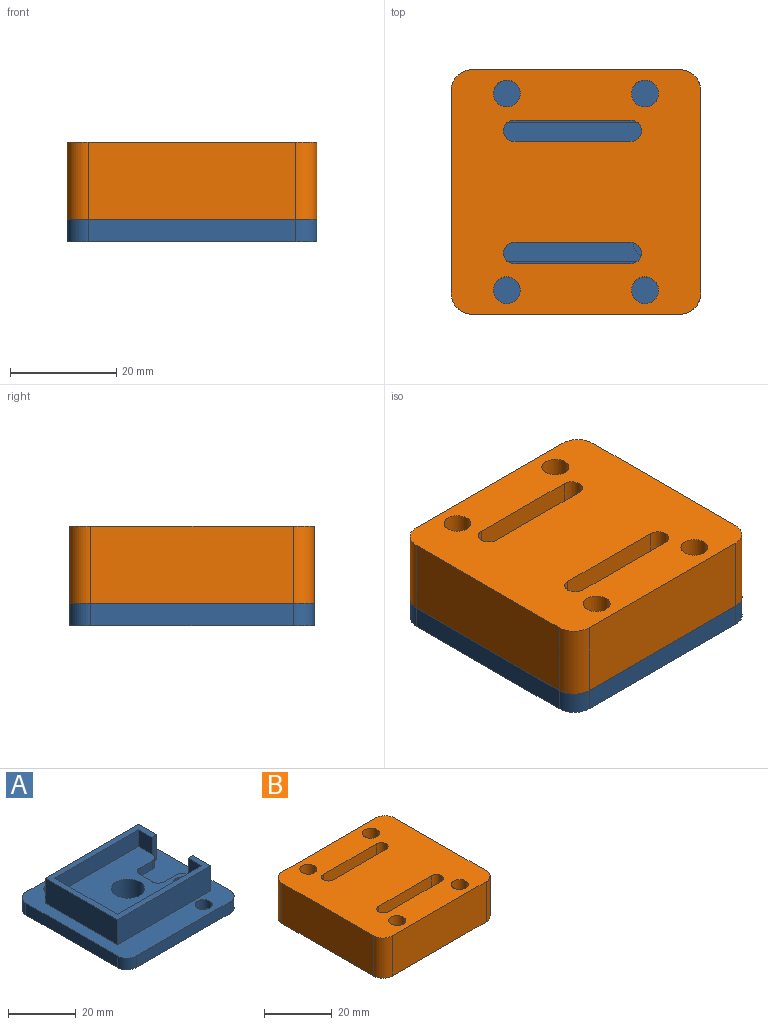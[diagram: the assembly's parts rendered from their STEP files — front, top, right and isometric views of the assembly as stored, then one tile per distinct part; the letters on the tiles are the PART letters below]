
ASSEMBLY  parts=2 mates=1
PART A: 38 faces, bbox 47x46x13.2 mm
  f0: plane 5x3mm, normal (0,-1,0), area 15mm2, adj f1,f6,f7,f21
  f1: cylinder r=2.5mm len=3mm, axis (0,0,-1), area 11.8mm2, adj f0,f7,f15,f21
  f2: cylinder r=2.5mm len=3mm, axis (0,0,-1), area 11.8mm2, adj f3,f7,f14,f21
  f3: plane 5x3mm, normal (0,1,0), area 15mm2, adj f2,f4,f7,f21
  f4: cylinder r=2.5mm len=3mm, axis (0,0,-1), area 11.8mm2, adj f3,f5,f7,f21
  f5: plane 5x3mm, normal (1,0,0), area 15mm2, adj f4,f6,f7,f21
  f6: cylinder r=2.5mm len=3mm, axis (0,0,-1), area 11.8mm2, adj f0,f5,f7,f21
  f7: plane 35x26mm, normal (0,0,1), area 706.3mm2, adj f0,f1,f2,f3,f4,f5,f6,f8
  f8: plane 35x6mm, normal (0,-1,0), area 210mm2, adj f7,f9,f11,f20
  f9: plane 26x6mm, normal (1,0,0), area 156mm2, adj f7,f8,f10,f20
  f10: plane 35x6mm, normal (0,1,0), area 210mm2, adj f7,f9,f12,f20
  f11: plane 6x5.5mm, normal (-1,0,0), area 33mm2, adj f7,f8,f15,f20
  f12: plane 6x5.5mm, normal (-1,0,0), area 33mm2, adj f7,f10,f14,f20
  f13: plane 9x7.5mm, normal (1,0,0), area 67.5mm2, adj f14,f19,f20,f21
  f14: plane 9x2mm, normal (0,1,0), area 18mm2, adj f2,f12,f13,f20,f21
  f15: plane 9x2mm, normal (0,-1,0), area 18mm2, adj f1,f11,f16,f20,f21
  f16: plane 9x7.5mm, normal (1,0,0), area 67.5mm2, adj f15,f17,f20,f21
  f17: plane 39x9mm, normal (0,1,0), area 351mm2, adj f16,f18,f20,f21
  f18: plane 30x9mm, normal (-1,0,0), area 270mm2, adj f17,f19,f20,f21
  f19: plane 39x9mm, normal (0,-1,0), area 351mm2, adj f13,f18,f20,f21
  f20: plane 39x30mm, normal (0,0,1), area 230mm2, adj f8,f9,f10,f11,f12,f13,f14,f15
  f21: plane 47x46mm, normal (0,0,1), area 1068.2mm2, adj f0,f1,f2,f3,f4,f5,f6,f13
  f22: plane 39x4.2mm, normal (0,1,0), area 163.8mm2, adj f21,f23,f31,f35
  f23: cylinder r=4mm len=4.2mm, axis (0,0,1), area 26.4mm2, adj f21,f22,f24,f35
  f24: plane 38x4.2mm, normal (-1,0,0), area 159.6mm2, adj f21,f23,f25,f35
  f25: cylinder r=4mm len=4.2mm, axis (0,0,1), area 26.4mm2, adj f21,f24,f26,f35
  f26: plane 39x4.2mm, normal (0,-1,0), area 163.8mm2, adj f21,f25,f27,f35
  f27: cylinder r=4mm len=4.2mm, axis (0,0,1), area 26.4mm2, adj f21,f26,f28,f35
  f28: plane 38x4.2mm, normal (1,0,0), area 159.6mm2, adj f21,f27,f31,f35
  f29: cylinder r=2.52mm len=5.05mm, axis (0,0,1), area 50.8mm2, adj f21,f33
  f30: cylinder r=2.52mm len=5.05mm, axis (0,0,1), area 50.8mm2, adj f21,f34
  f31: cylinder r=4mm len=4.2mm, axis (0,0,1), area 26.4mm2, adj f21,f22,f28,f35
  f32: cylinder r=4.9mm len=9.8mm, axis (0,0,-1), area 221.7mm2, adj f7,f35
  f33: plane 5.05x5.05mm, normal (0,0,1), area 20mm2, adj f29
  f34: plane 5.05x5.05mm, normal (0,0,1), area 20mm2, adj f30
  f35: plane 47x46mm, normal (0,0,-1), area 2072.8mm2, adj f22,f23,f24,f25,f26,f27,f28,f31
  f36: cylinder r=3mm len=6mm, axis (0,0,1), area 56.5mm2, adj f7,f37
  f37: plane 6x6mm, normal (0,0,1), area 28.3mm2, adj f36
PART B: 32 faces, bbox 47x46x14.5 mm
  f0: plane 39.3x9.5mm, normal (0,-1,0), area 373.4mm2, adj f1,f14,f15,f16
  f1: plane 10.15x9.5mm, normal (-1,0,0), area 74mm2, adj f0,f2,f15,f16,f27
  f2: plane 7x3.85mm, normal (0,-1,0), area 27mm2, adj f1,f10,f15,f27
  f3: cylinder r=4mm len=14.5mm, axis (0,0,-1), area 91.1mm2, adj f4,f10,f15,f21
  f4: plane 39x14.5mm, normal (0,1,0), area 565.5mm2, adj f3,f5,f15,f21
  f5: cylinder r=4mm len=14.5mm, axis (0,0,-1), area 91.1mm2, adj f4,f6,f15,f21
  f6: plane 38x14.5mm, normal (-1,0,0), area 551mm2, adj f5,f7,f15,f21
  f7: cylinder r=4mm len=14.5mm, axis (0,0,-1), area 91.1mm2, adj f6,f8,f15,f21
  f8: plane 39x14.5mm, normal (0,-1,0), area 565.5mm2, adj f7,f9,f15,f21
  f9: cylinder r=4mm len=14.5mm, axis (0,0,-1), area 91.1mm2, adj f8,f10,f15,f21
  f10: plane 38x14.5mm, normal (1,0,0), area 411.2mm2, adj f2,f3,f9,f11,f15,f16,f21,f26
  f11: plane 7x3.85mm, normal (0,1,0), area 27mm2, adj f10,f12,f15,f26
  f12: plane 10.15x9.5mm, normal (-1,0,0), area 74mm2, adj f11,f13,f15,f16,f26
  f13: plane 39.3x9.5mm, normal (0,1,0), area 373.4mm2, adj f12,f14,f15,f16
  f14: plane 30.3x9.5mm, normal (1,0,0), area 287.9mm2, adj f0,f13,f15,f16
  f15: plane 47x46mm, normal (0,0,-1), area 819.6mm2, adj f0,f1,f2,f3,f4,f5,f6,f7
  f16: plane 43.15x30.3mm, normal (0,0,-1), area 1028.2mm2, adj f0,f1,f10,f12,f13,f14,f17,f18
  f17: plane 22x5mm, normal (0,-1,0), area 110mm2, adj f16,f21,f22,f23
  f18: plane 22x5mm, normal (0,1,0), area 110mm2, adj f16,f21,f24,f25
  f19: plane 22x5mm, normal (0,-1,0), area 110mm2, adj f16,f21,f24,f25
  f20: plane 22x5mm, normal (0,1,0), area 110mm2, adj f16,f21,f22,f23
  f21: plane 47x46mm, normal (0,0,1), area 1867mm2, adj f3,f4,f5,f6,f7,f8,f9,f10
  f22: cylinder r=2mm len=5mm, axis (0,0,-1), area 31.4mm2, adj f16,f17,f20,f21
  f23: cylinder r=2mm len=5mm, axis (0,0,1), area 31.4mm2, adj f16,f17,f20,f21
  f24: cylinder r=2mm len=5mm, axis (0,0,-1), area 31.4mm2, adj f16,f18,f19,f21
  f25: cylinder r=2mm len=5mm, axis (0,0,1), area 31.4mm2, adj f16,f18,f19,f21
  f26: cylinder r=2.5mm len=3.85mm, axis (1,0,0), area 15.1mm2, adj f10,f11,f12,f16
  f27: cylinder r=2.5mm len=3.85mm, axis (-1,0,0), area 15.1mm2, adj f1,f2,f10,f16
  f28: cylinder r=2.52mm len=14.5mm, axis (0,0,-1), area 230mm2, adj f15,f21
  f29: cylinder r=2.52mm len=14.5mm, axis (0,0,-1), area 230mm2, adj f15,f21
  f30: cylinder r=2.52mm len=14.5mm, axis (0,0,-1), area 230mm2, adj f15,f21
  f31: cylinder r=2.52mm len=14.5mm, axis (0,0,-1), area 230mm2, adj f15,f21
PLACE A t=(-48.77,-70.72,20.04)mm
PLACE B t=(-127.1,-63.33,20.04)mm
MATE slider A.f29 <-> B.f29  axis (0,0,1) through (-30.43,-68.23,20.04)mm
